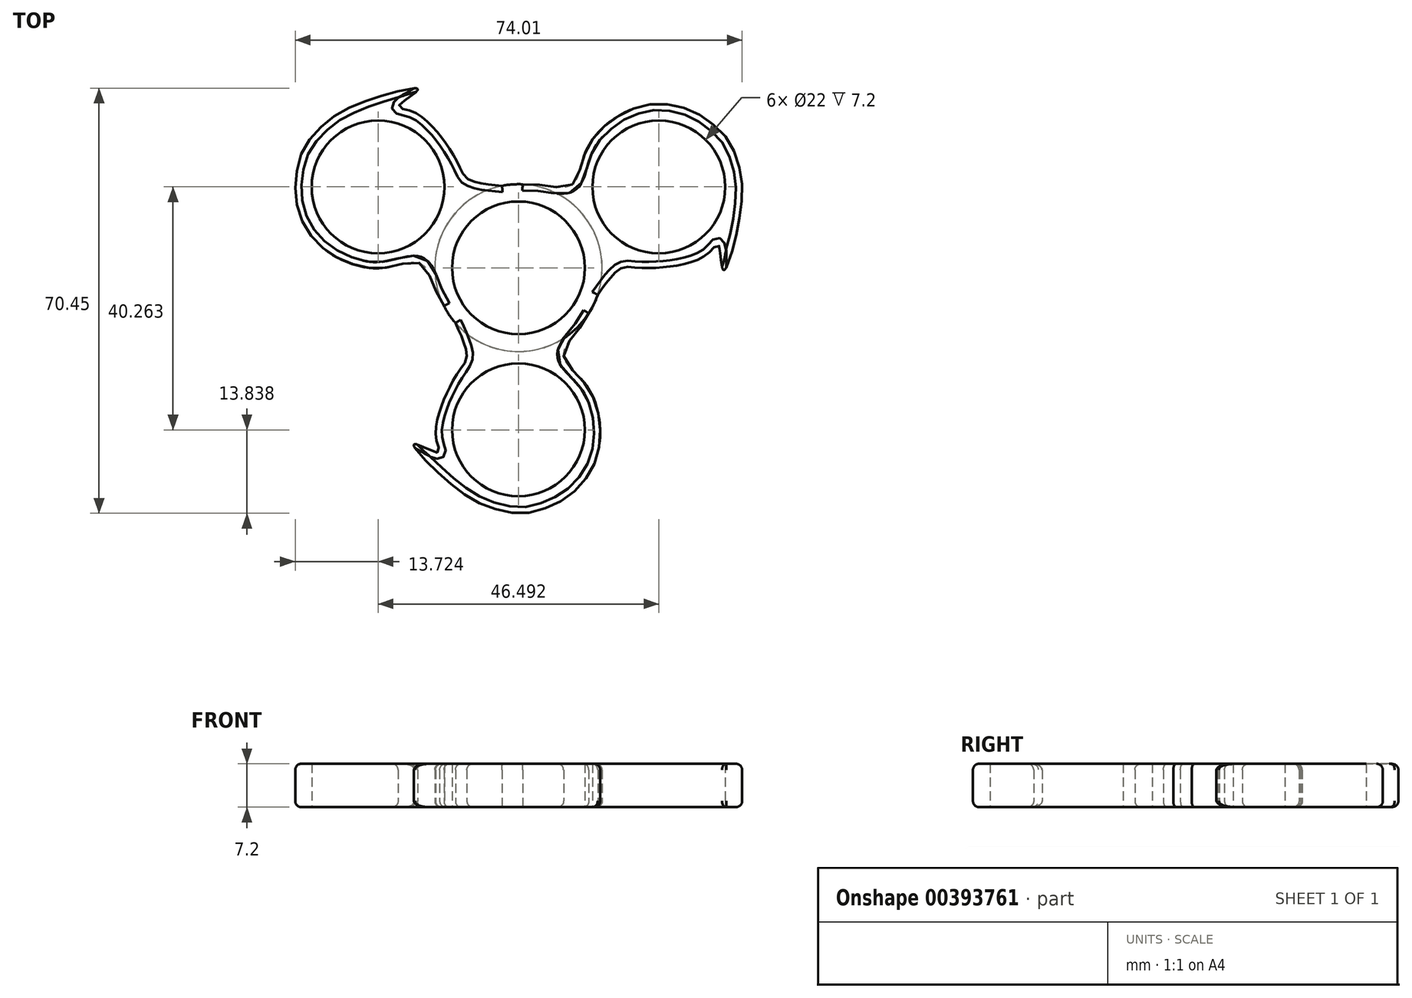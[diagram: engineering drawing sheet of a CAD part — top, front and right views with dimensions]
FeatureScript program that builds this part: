
annotation { "Feature Type Name" : "Feature", "Feature Type Description" : "" }
export const myFeature = defineFeature(function(context is Context, id is Id, definition is map)
    precondition{}
    {
        {
            var Q0;
            Q0=qCreatedBy(makeId("Top.planeOp"),FACE);
            var sketch = newSketch(context, id + "F0", { "sketchPlane" : qUnion([Q0])});
            skCircle(sketch, "E0", {"center": v(0, 0) * mm, "radius": 11 * mm});
            skCircle(sketch, "E1", {"center": v(0, -26.84) * mm, "radius": 11 * mm});
            skCircle(sketch, "E2", {"center": v(0, 0) * mm, "radius": 13.86 * mm});
            skLineSegment(sketch, "E3", {"start": v(0, 0) * mm, "end": v(0, -53.68) * mm, "construction": true});
            skFitSpline(sketch, "E4", {"points": [v(11.65, -7.52) * mm, v(9.7, -10.52) * mm, v(7.48, -14.55) * mm, v(11.48, -19.8) * mm, v(13.37, -29.5) * mm, v(10.69, -35.54) * mm, v(6.87, -38.72) * mm, v(2.5, -40.42) * mm, v(-0.17, -40.67) * mm, v(-3.15, -40.17) * mm, v(-9.64, -37.02) * mm, v(-17.24, -29.21) * mm, v(-13.24, -30.62) * mm, v(-13.7, -27.85) * mm, v(-9.88, -17.15) * mm, v(-8.54, -14.62) * mm, v(-10.42, -9.14) * mm], "startDerivative": vector(-32.29, -56) * mm, "endDerivative": vector(-44.62, 97.98) * mm});
            skSolve(sketch);
        }
        {
            var Q0;
            Q0=qSketchRegion(id+"F0",true);
            extrude(context, id + "F1", {"entities" : qUnion([Q0]), "depth" : 7.2 * mm});
        }
        {
            var Q0;
            Q0=makeQuery(id+"F1.opExtrude","CAP_EDGE",EDGE,{"disambiguationData":[OSD([sQuery(id+"F0.wireOp",EDGE,"E4")])],"isStart":true});
            var Q1;
            Q1=makeQuery(id+"F1.opExtrude","CAP_EDGE",EDGE,{"disambiguationData":[OSD([sQuery(id+"F0.wireOp",EDGE,"E2")])],"isStart":true});
            var Q2;
            Q2=makeQuery(id+"F1.opExtrude","CAP_EDGE",EDGE,{"disambiguationData":[OSD([sQuery(id+"F0.wireOp",EDGE,"E4")])],"isStart":false});
            var Q3;
            Q3=makeQuery(id+"F1.opExtrude","CAP_EDGE",EDGE,{"disambiguationData":[OSD([sQuery(id+"F0.wireOp",EDGE,"E2")])],"isStart":false});
            fillet(context, id + "F2", {"entities" : qUnion([Q0, Q1, Q2, Q3]), "radius" : 1.02 * mm, "tangentPropagation" : true, "allowEdgeOverflow" : false});
        }
        {
            var Q0;
            Q0=makeQuery(id+"F1.opExtrude","SWEPT_BODY",BODY,{"disambiguationData":[OSD([sQuery(id+"F0.wireOp",EDGE,"E0"),sQuery(id+"F0.wireOp",EDGE,"E1"),sQuery(id+"F0.wireOp",EDGE,"E2"),sQuery(id+"F0.wireOp",EDGE,"E4")])]});
            var Q1;
            Q1=makeQuery(id+"F1.opExtrude","CAP_EDGE",EDGE,{"disambiguationData":[OSD([sQuery(id+"F0.wireOp",EDGE,"E0")])],"isStart":false});
            circularPattern(context, id + "F3", {"entities" : qUnion([Q0]), "axis" : qUnion([Q1]), "angle" : 360 * degree, "instanceCount" : 3, "oppositeDirection" : true, "equalSpace" : true});
        }
    });
